# Revit family: Table-Casual-Naughtone-Dalby_SQ_Side
name_source: partatom
category: Furniture
revit_build: Autodesk Revit 2015 (Build: 20150704_0715(x64)
units: mm (PartAtom-declared; Revit-internal decimal feet)

## types (1)
- 350mmx350mmx550mm
    AdditionalMaterials = Additional material and finish options available. Please contact Naughtone direct for further information.
    Assembly Code = E2020
    AssetIdentifier = DAL-350-SQ-SIDE
    AssetType = Movable
    BIMObjectName = Table-Casual-Naughtone-Dalby_SQ_Side
    BarCode = 0.000000
    Category = 40.50.21.58 : Occasional Tables
    CodePerformance = FISP Certified; ISO14001 Certified
    Color = White
    ComponentDescription = The Dalby table will inject warmth and quality into an interior without raising any eyebrows. Dalby provides a practical, robust surface and maximised leg positions for clear, useable access all round the table.
    Constituents = Wood Top; Solid Oak frame
    Cost = 0 $
    Description = Dalby Side Table
    DurationUnit = Years
    ExpectedLife = 15-20
    Finish = Polyster powder coat; various top finishes available
    Keynote = 40.50.21.58
    Manufacturer = Naughtone
    ManufacturerAddressUK = 201 Pannal Business Park, Station Road, Harrogate, HG3 1JL
    Material = MFMDF Top; Solid Oak Legs
    Model = DAL-350-SQ-SIDE
    ModelNumber = DAL-350-SQ-SIDE
    ModelReference = Dalby Side Table
    NBSReference = 40.50.21.58
    Name = 350mmx350mmx550mm, Dalby Side Table
    NominalHeight = 550 mm
    NominalLength = 350 mm  [stored 1.14829 ft]
    NominalWidth = 350 mm  [stored 1.14829 ft]
    Product URL = http://www.naughtone.com
    ProductInformation = http://www.naughtone.com
    ReplacementCost = 0.00
    SerialNumber = 0.000000
    Shape = Rectangular
    Size = 350mmx350mmx550mm
    SustainabilityPerformance = 89.64% reusable content
    TagNumber = 0.000000
    Type Comments = 350x350x550
    TypeName = Table-Casual-Naughtone-Dalby_SQ_Side
    URL = http://www.naughtone.com
    Uniclass2015 = 40.50.21.58
    Version = 1
    WarrantyDescription = 5 year warranty
    WarrantyDurationLabor = 5
    WarrantyDurationParts = 5
    WarrantyDurationUnit = Years
    _BIMspec_GUID = 0
    _current revision = 1
    _distributed by = www.bimbox.co.uk

note: [stored X ft] marks values corroborated as IEEE doubles in the binary element streams (Revit-internal decimal feet)

## geometry (parser evidence)
native form markers: Sweep x3
no freeform markers — native parametric forms only
